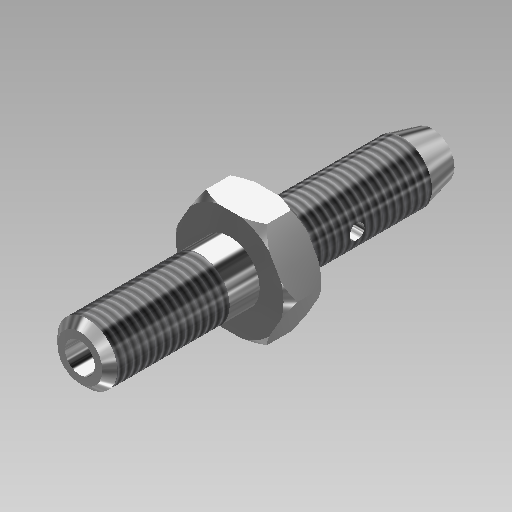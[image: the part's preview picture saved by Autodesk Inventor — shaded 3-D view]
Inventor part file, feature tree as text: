
AUTODESK INVENTOR PART (.ipt)
format: ipt  version: 2018.1 (Build 221171000, 171)  size: 220,160 bytes
history: native  units: in
note: dims shown in document units (in); Inventor stores cm internally (conversion verified against a paired STEP export)
features: sketch x6, extrude x5, chamfer x2, thread x2, plane x1, revolve x1
ambient origin geometry x8: Origin, YZ Plane, XZ Plane, XY Plane, X Axis, Y Axis, Z Axis, Center Point
bodies: Solid1 (feature_tree)
feature tree (17):
  extrude  "Extrusion1"  Depth=0.3937in TaperAngle=0.0deg
  extrude  "Extrusion2"  Depth=0.0197in
  chamfer  "Chamfer1"  Distance=0.4331in
  thread  "Thread1"  [1 undecoded]
  extrude  "Extrusion3"  Depth=0.0197in
  thread  "Thread2"  [1 undecoded]
  chamfer  "Chamfer2"  Distance=0.9843in
  plane  "Work Plane1"
  revolve  "Revolution1"  [1 undecoded]
  extrude  "Extrusion4"  [1 undecoded]
  extrude  "Extrusion5"  [1 undecoded]
  sketch  "Sketch1"  dims[d1=0.0984in d2=0.0in d4=0.3937in d5=0.0in]
  sketch  "Sketch2"  dims[d6=0.0197in d7=0.0787in d8=45.0deg d9=0.315in d10=0.0787in d12=0.4331in d13=0.0in d14=0.315in d15=0.0787in]
  sketch  "Sketch3"  dims[d16=0.0197in d17=0.0787in d18=45.0deg d23=0.0807in d24=90.0deg]
  sketch  "Sketch5"  dims[d25=0.0787in d26=0.9843in d27=0.0in]
  sketch  "Sketch6"  dims[d30=0.1969in d31=0.0in]
  sketch  "Sketch7"
note: 5 required parameter values undecoded (feature->parameter linkage not recoverable at this tier; creation-order binding heuristic only, values carry confidence <= 0.55)
